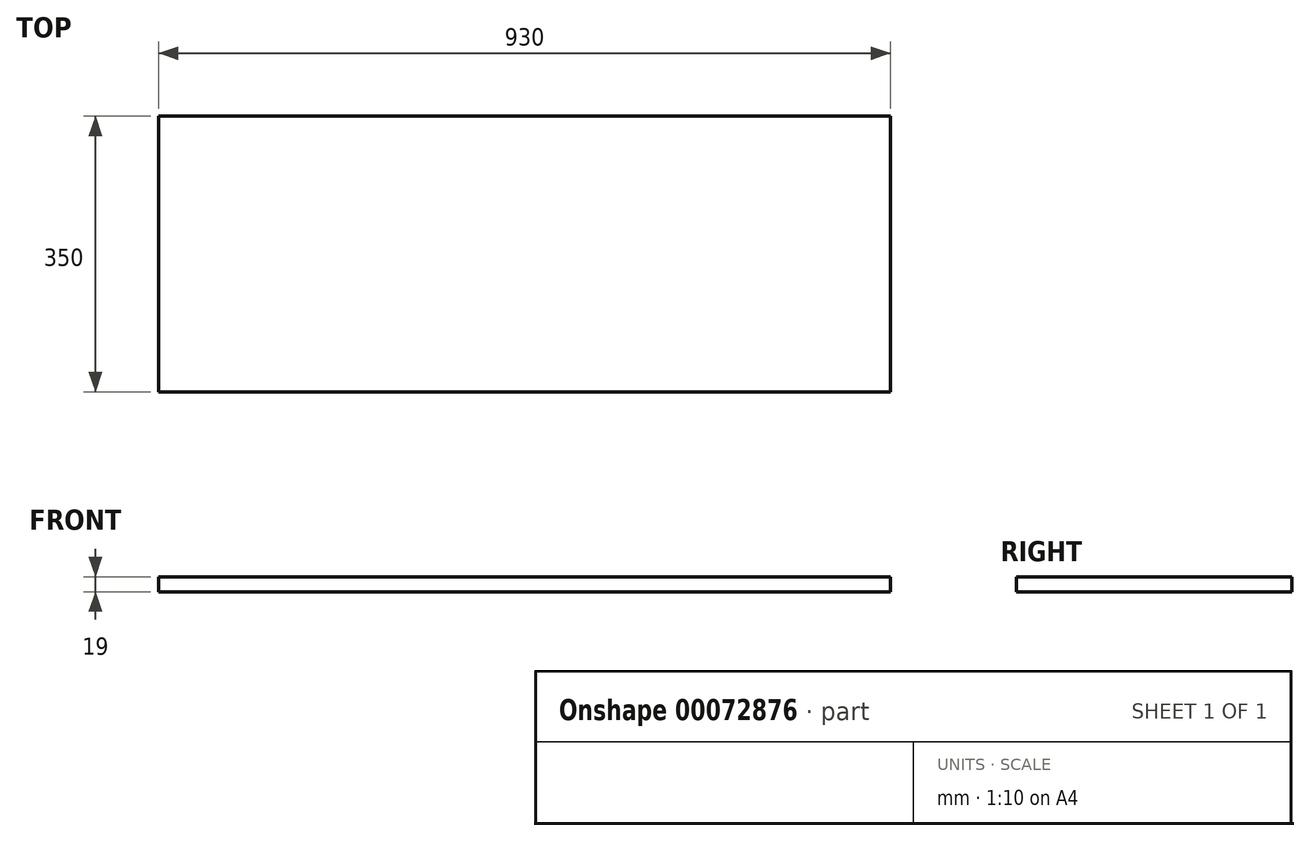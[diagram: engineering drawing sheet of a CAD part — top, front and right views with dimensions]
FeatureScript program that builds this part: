
annotation { "Feature Type Name" : "Feature", "Feature Type Description" : "" }
export const myFeature = defineFeature(function(context is Context, id is Id, definition is map)
    precondition{}
    {
        {
            var Q0;
            Q0=qCreatedBy(makeId("Top.planeOp"),FACE);
            var sketch = newSketch(context, id + "F0", { "sketchPlane" : qUnion([Q0])});
            skLineSegment(sketch, "E0.bottom", {"start": v(0, 0) * mm, "end": v(930, 0) * mm});
            skLineSegment(sketch, "E0.top", {"start": v(0, -350) * mm, "end": v(930, -350) * mm});
            skLineSegment(sketch, "E0.left", {"start": v(0, 0) * mm, "end": v(0, -350) * mm});
            skLineSegment(sketch, "E0.right", {"start": v(930, 0) * mm, "end": v(930, -350) * mm});
            skSolve(sketch);
        }
        {
            var Q0;
            Q0=makeQuery(id+"F0.imprint","IMPRINT",FACE,{"disambiguationData":[TD([[makeQuery(id+"F0.imprint","IMPRINT",EDGE,{"derivedFrom":sQuery(id+"F0.wireOp",EDGE,"E0.bottom")}),-1.0]])]});
            extrude(context, id + "F1", {"entities" : qUnion([Q0]), "depth" : 19 * mm});
        }
    });
